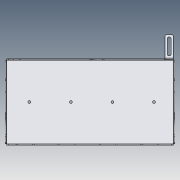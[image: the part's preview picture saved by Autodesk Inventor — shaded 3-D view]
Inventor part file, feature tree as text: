
AUTODESK INVENTOR PART (.ipt)
format: ipt  version: 2020.5 (Build 245400000, 400)  size: 579,584 bytes
history: native  units: mm
features: sketch x12, other x11, sheet_metal_op x7, projected_geometry x6, pattern_linear x1, hole x1, extrude x1, chamfer x1
ambient origin geometry x8: Origin, YZ Plane, XZ Plane, XY Plane, X Axis, Y Axis, Z Axis, Center Point
bodies: Solid1 (feature_tree)
feature tree (40):
  sheet_metal_op  "Face1"
  sheet_metal_op  "Flange1"
  pattern_linear  "Rectangular Pattern1"  Count1=6  [1 undecoded]
  hole  "Hole1"  [1 undecoded]
  extrude  "Extrusion1"  Depth=18.0mm
  sheet_metal_op  "Flange3"
  chamfer  "Corner Round3"
  sketch  "Sketch2"  dims[d0=202.1mm]
  other  "Plate1"
  sketch  "Sketch3"  dims[d1=102.0mm]
  other  "Plate2"
  sheet_metal_op  "Bend1"
  sheet_metal_op  "Corner1"
  sketch  "Sketch4"  dims[d2=1.0mm]
  projected_geometry  "Projected Loop1"
  sketch  "Sketch6"  dims[d3=1.0mm]
  projected_geometry  "Projected Loop3"
  sketch  "Sketch7"  dims[d4=0.5mm]
  projected_geometry  "Projected Loop4"
  sketch  "Sketch8"  dims[d5=2.0mm]
  projected_geometry  "Projected Loop5"
  sketch  "Sketch9"  dims[d6=1.0mm]
  sketch  "Sketch11"  dims[d7=69.4mm d8=90.0deg d9=1.0mm]
  sketch  "Sketch12"  dims[d10=4.0mm]
  projected_geometry  "Projected Loop6"
  sketch  "Sketch14"  dims[d11=1.0mm]
  other  "Plate4"
  sheet_metal_op  "Bend3"
  sheet_metal_op  "Corner3"
  sketch  "Sketch15"  dims[d12=1.0mm]
  projected_geometry  "Projected Loop7"
  sketch  "Sketch16"  dims[d13=18.0mm d14=60.0mm d17=28.293mm d19=18.0mm d20=60.0mm d21=78.293mm d22=18.0mm d23=60.0mm d24=128.393mm d25=18.0mm d26=60.0mm d27=178.393mm d28=1.0mm d29=0.0mm d38=13.5mm d40=8.373mm d41=1.0mm d42=0.0mm d51=2.0mm d53=2.0mm d55=35.293mm d56=44.043mm d61=94.043mm d62=85.293mm d64=4.0mm d65=4.0mm d66=60.0mm d68=8.0mm d69=4.0mm d70=23.293mm d72=20.0mm d74=100.1mm d75=60.0mm d76=12.92mm d78=30.833mm d79=1.0mm d80=0.0mm d82=23.232mm d88=1.0mm d89=0.0mm d91=70.0mm d92=25.0mm d93=12.5mm d94=29.0mm d95=38.65mm d96=40.306mm d97=43.025mm d98=41.55mm d99=43.025mm d100=41.55mm d101=29.0mm d102=23.251086mm d108=50.0mm d109=23.0mm d110=50.0mm d111=100.1mm d112=150.1mm d113=27.0mm d114=3.5mm d115=6.0mm d116=4.0mm d117=2.0mm d118=90.0deg d119=1.0mm d120=20.594885mm d123=1.0mm d124=1.0mm d125=200.1mm d126=200.685786mm d130=10.0mm d131=27.560906mm d132=30.0mm d133=1.0mm d134=0.0mm d135=10.0mm d136=1.0mm d137=1.0mm d138=0.0mm d149=1.0mm d150=0.5mm d151=2.0mm d152=1.0mm d153=30.0mm d154=90.0deg d155=1.0mm d156=4.0mm d157=1.0mm d158=1.0mm d160=5.0mm d161=18.0mm d162=1.0mm d163=0.0mm d164=35.5mm d165=8.373mm d166=1.0mm d167=0.0mm d168=2.0mm]
  other  "Cut1"
  other  "Cut2"
  other  "Cut3"
  other  "Cut4"
  other  "Cut5"
  other  "Cut6"
  other  "Cut7"
  other  "Definition1"
note: 2 required parameter values undecoded (feature->parameter linkage not recoverable at this tier; creation-order binding heuristic only, values carry confidence <= 0.55)
